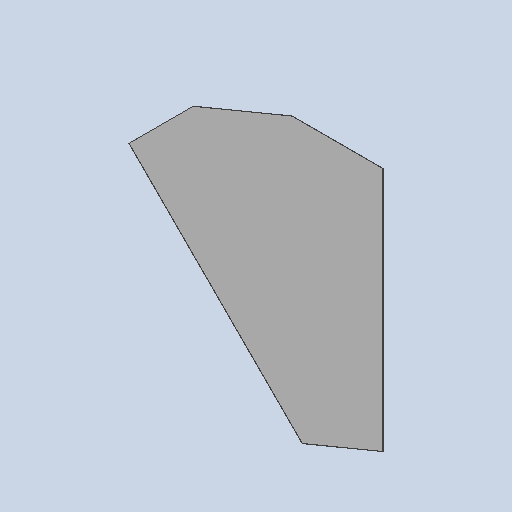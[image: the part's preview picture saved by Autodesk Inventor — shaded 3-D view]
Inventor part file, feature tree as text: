
AUTODESK INVENTOR PART (.ipt)
format: ipt  version: 2025 (Build 290162010, 162A)  size: 98,816 bytes
history: native  units: mm
features: other x3, sketch x1
ambient origin geometry x8: Origin, YZ Plane, XZ Plane, XY Plane, X Axis, Y Axis, Z Axis, Center Point
bodies: Solid1 (feature_tree)
feature tree (4):
  other  "ДМС 207 Сетка кассеты"
  other  "Solid1::ДМС 207 Сетка кассеты"
  other  "TaggingFeature1"
  sketch  "Sketch1"  dims[d0=10.0mm d1=0.5mm]
